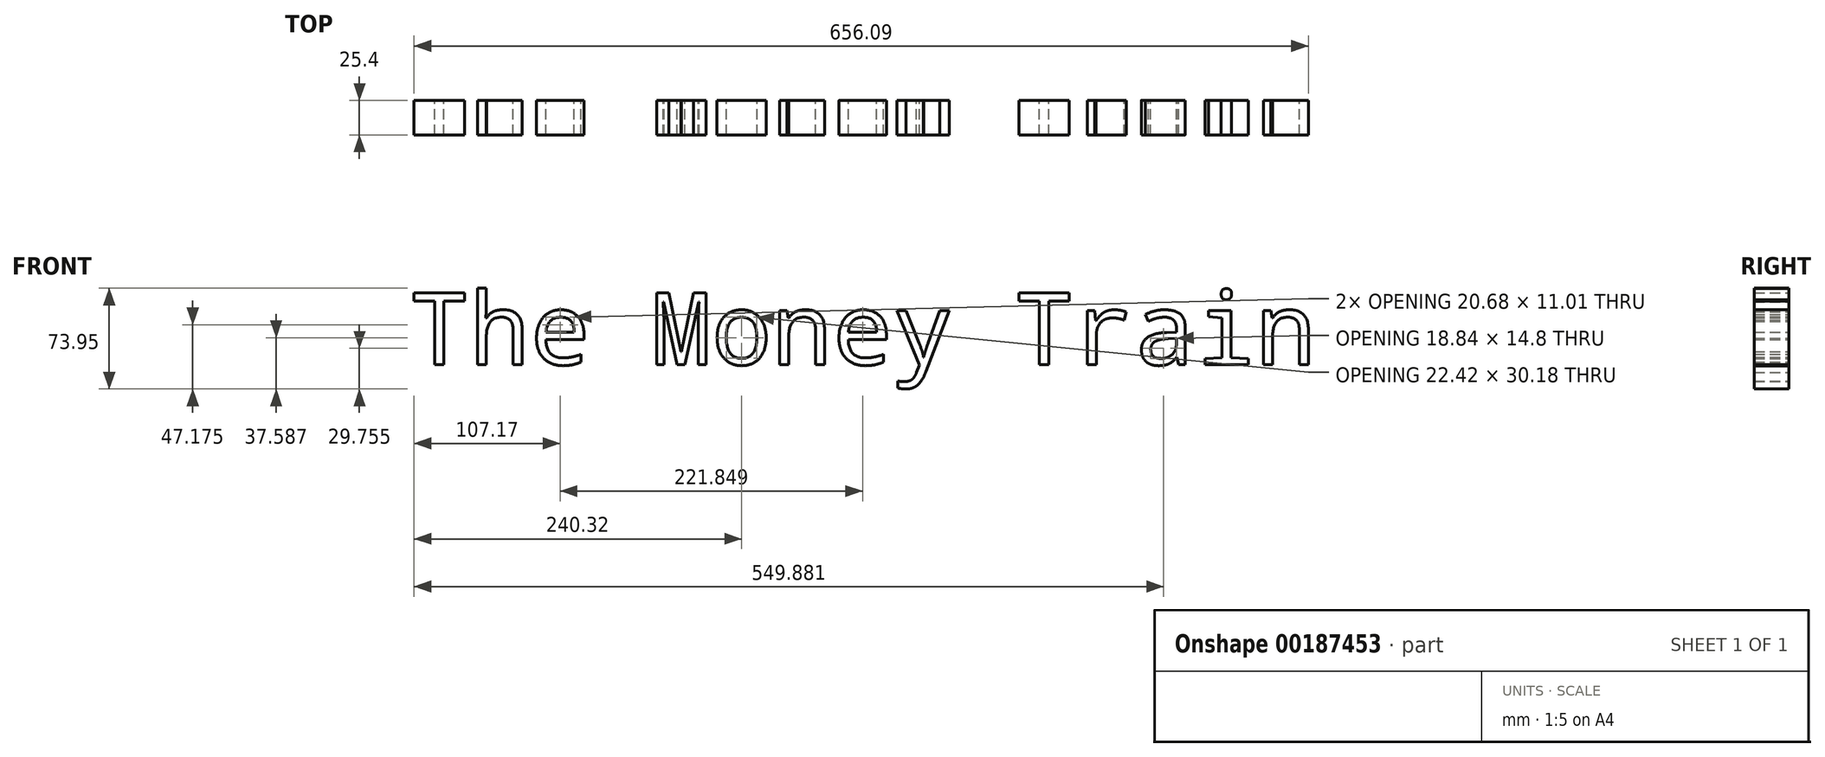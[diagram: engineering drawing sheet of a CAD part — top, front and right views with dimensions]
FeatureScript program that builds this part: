
annotation { "Feature Type Name" : "Feature", "Feature Type Description" : "" }
export const myFeature = defineFeature(function(context is Context, id is Id, definition is map)
    precondition{}
    {
        {
            var Q0;
            Q0=qCreatedBy(makeId("Front.planeOp"),FACE);
            var sketch = newSketch(context, id + "F0", { "sketchPlane" : qUnion([Q0])});
            skLineSegment(sketch, "E0", {"start": v(-76.59, -55.98) * mm, "end": v(62.74, -55.98) * mm, "construction": true});
            skLineSegment(sketch, "E1", {"start": v(-76.59, 0) * mm, "end": v(61.57, 0) * mm, "construction": true});
            skLineSegment(sketch, "E2", {"start": v(-69.58, 0) * mm, "end": v(-69.58, -55.98) * mm});
            skLineSegment(sketch, "E3", {"start": v(-69.58, -55.98) * mm, "end": v(-66.08, -55.98) * mm});
            skText(sketch, "E4", { "text": "The Money Train", "fontName": "DroidSansMono.ttf"});
            const initialGuessF0  = {"E4": [-0.6081, -0.05598, 1, 0, 0.05323]};
            skSetInitialGuess(sketch, initialGuessF0);
            skSolve(sketch);
        }
        {
            var Q0;
            Q0 = qSketchRegion(id + "F0", true);
            extrude(context, id + "F1", {"entities" : qUnion([Q0]), "depth" : 25.4 * mm});
        }
    });
